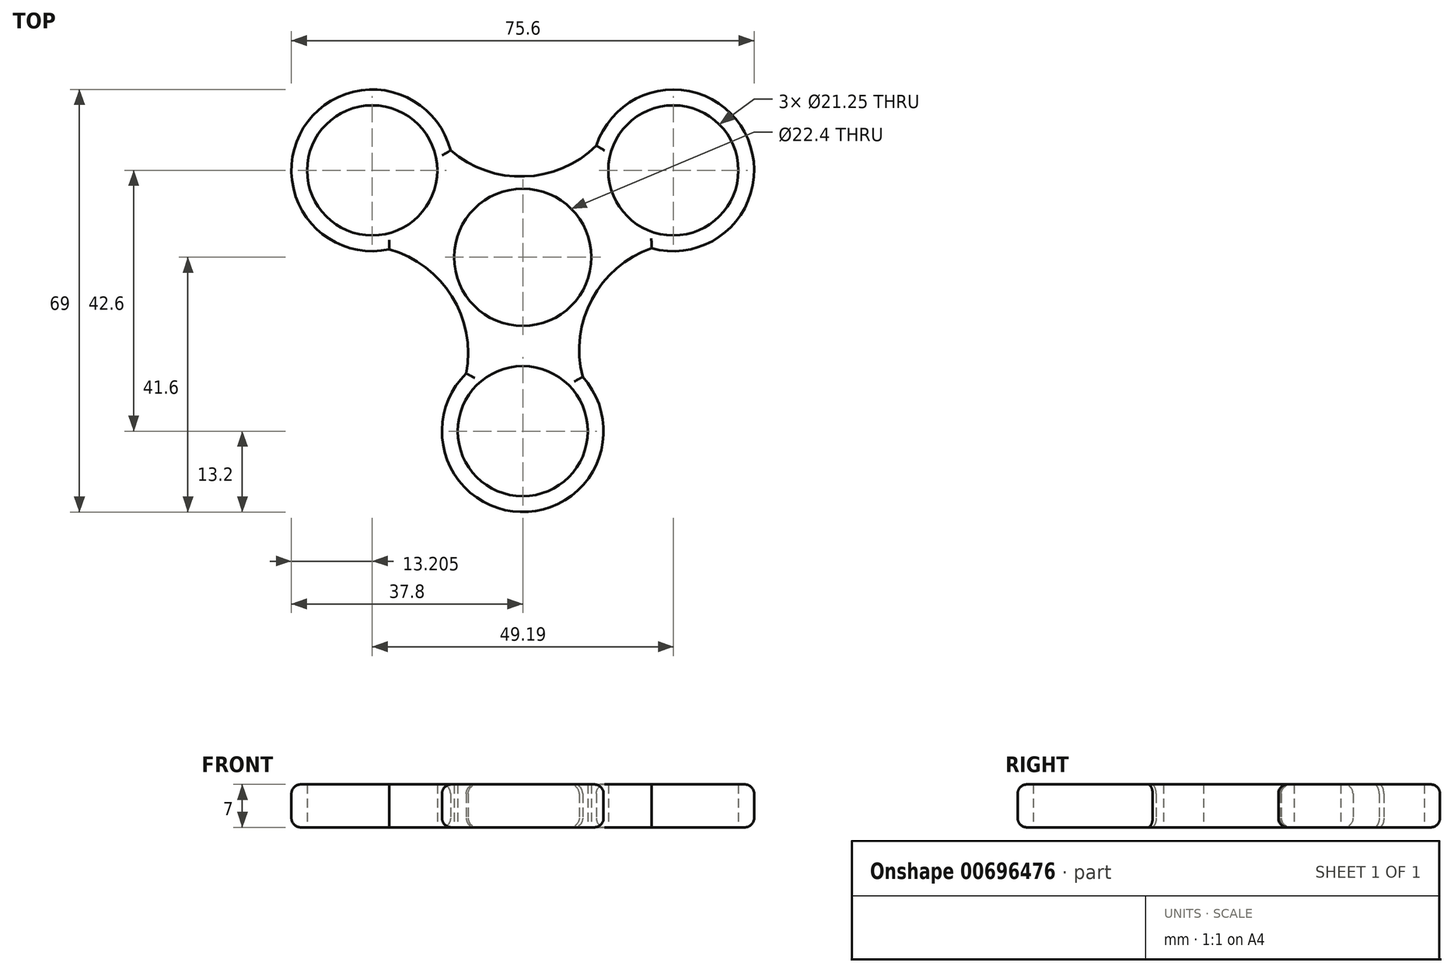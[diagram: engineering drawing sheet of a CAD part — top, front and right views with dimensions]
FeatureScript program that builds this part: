
annotation { "Feature Type Name" : "Feature", "Feature Type Description" : "" }
export const myFeature = defineFeature(function(context is Context, id is Id, definition is map)
    precondition{}
    {
        {
            var Q0;
            Q0=qCreatedBy(makeId("Top.planeOp"),FACE);
            var sketch = newSketch(context, id + "F0", { "sketchPlane" : qUnion([Q0])});
            skCircle(sketch, "E0", {"center": v(0, 0) * mm, "radius": 11.2 * mm});
            skArc(sketch, "E1", {"start": v(-11.43, -6.6) * mm, "mid": v(-11.37, -6.71) * mm, "end": v(-11.3, -6.83) * mm});
            skArc(sketch, "E2", {"start": v(-9.23, -18.96) * mm, "mid": v(-0.4, -41.6) * mm, "end": v(9.78, -19.54) * mm});
            skCircle(sketch, "E3", {"center": v(0, -28.4) * mm, "radius": 10.62 * mm});
            skPoint(sketch, "E4.start.orphan", {"position": v(0, -13.2) * mm});
            skCircle(sketch, "E5.1.0", {"center": v(24.6, 14.2) * mm, "radius": 10.62 * mm});
            skArc(sketch, "E5.1.1", {"start": v(21.04, 1.49) * mm, "mid": v(36.22, 20.45) * mm, "end": v(12.03, 18.24) * mm});
            skCircle(sketch, "E5.2.0", {"center": v(-24.6, 14.2) * mm, "radius": 10.62 * mm});
            skArc(sketch, "E5.2.1", {"start": v(-11.8, 17.47) * mm, "mid": v(-35.82, 21.14) * mm, "end": v(-21.81, 1.3) * mm});
            skArc(sketch, "E6", {"start": v(-11.8, 17.47) * mm, "mid": v(0.26, 13.2) * mm, "end": v(12.03, 18.24) * mm});
            skArc(sketch, "E7.1.0", {"start": v(-9.23, -18.96) * mm, "mid": v(-11.57, -6.38) * mm, "end": v(-21.81, 1.3) * mm});
            skArc(sketch, "E7.2.0", {"start": v(21.04, 1.49) * mm, "mid": v(11.3, -6.83) * mm, "end": v(9.78, -19.54) * mm});
            skArc(sketch, "E8.trimOffspring", {"start": v(0, 13.2) * mm, "mid": v(-0.13, 13.2) * mm, "end": v(-0.26, 13.2) * mm});
            skArc(sketch, "E9.trimOffspring", {"start": v(11.43, -6.6) * mm, "mid": v(11.5, -6.49) * mm, "end": v(11.56, -6.37) * mm});
            skPoint(sketch, "E10.start.orphan", {"position": v(13.2, 0) * mm});
            skPoint(sketch, "E11.start.orphan", {"position": v(-13.2, 0) * mm});
            skPoint(sketch, "E12.start.orphan", {"position": v(0, 15.2) * mm});
            skSolve(sketch);
        }
        {
            var Q0;
            Q0=makeQuery(id+"F0.imprint","IMPRINT",FACE,{"disambiguationData":[TD([[makeQuery(id+"F0.imprint","IMPRINT",EDGE,{"derivedFrom":sQuery(id+"F0.wireOp",EDGE,"E0")}),-1.0]])]});
            extrude(context, id + "F1", {"entities" : qUnion([Q0]), "depth" : 7 * mm, "offsetDistance" : 25 * mm});
        }
        {
            var Q0;
            Q0=makeQuery(id+"F1.opExtrude","CAP_EDGE",EDGE,{"disambiguationData":[OSD([sQuery(id+"F0.wireOp",EDGE,"E5.2.1")])],"isStart":false});
            var Q1;
            Q1=makeQuery(id+"F1.opExtrude","CAP_EDGE",EDGE,{"disambiguationData":[OSD([sQuery(id+"F0.wireOp",EDGE,"E6")])],"isStart":false});
            var Q2;
            Q2=makeQuery(id+"F1.opExtrude","CAP_EDGE",EDGE,{"disambiguationData":[OSD([sQuery(id+"F0.wireOp",EDGE,"E7.1.0")])],"isStart":false});
            var Q3;
            Q3=makeQuery(id+"F1.opExtrude","CAP_EDGE",EDGE,{"disambiguationData":[OSD([sQuery(id+"F0.wireOp",EDGE,"E5.1.1")])],"isStart":false});
            var Q4;
            Q4=makeQuery(id+"F1.opExtrude","CAP_EDGE",EDGE,{"disambiguationData":[OSD([sQuery(id+"F0.wireOp",EDGE,"E7.2.0")])],"isStart":false});
            var Q5;
            Q5=makeQuery(id+"F1.opExtrude","CAP_EDGE",EDGE,{"disambiguationData":[OSD([sQuery(id+"F0.wireOp",EDGE,"E2")])],"isStart":false});
            var Q6;
            Q6=makeQuery(id+"F1.opExtrude","CAP_EDGE",EDGE,{"disambiguationData":[OSD([sQuery(id+"F0.wireOp",EDGE,"E5.2.1")])],"isStart":true});
            var Q7;
            Q7=makeQuery(id+"F1.opExtrude","CAP_EDGE",EDGE,{"disambiguationData":[OSD([sQuery(id+"F0.wireOp",EDGE,"E6")])],"isStart":true});
            var Q8;
            Q8=makeQuery(id+"F1.opExtrude","CAP_EDGE",EDGE,{"disambiguationData":[OSD([sQuery(id+"F0.wireOp",EDGE,"E7.1.0")])],"isStart":true});
            var Q9;
            Q9=makeQuery(id+"F1.opExtrude","CAP_EDGE",EDGE,{"disambiguationData":[OSD([sQuery(id+"F0.wireOp",EDGE,"E2")])],"isStart":true});
            var Q10;
            Q10=makeQuery(id+"F1.opExtrude","CAP_EDGE",EDGE,{"disambiguationData":[OSD([sQuery(id+"F0.wireOp",EDGE,"E7.2.0")])],"isStart":true});
            var Q11;
            Q11=makeQuery(id+"F1.opExtrude","CAP_EDGE",EDGE,{"disambiguationData":[OSD([sQuery(id+"F0.wireOp",EDGE,"E5.1.1")])],"isStart":true});
            fillet(context, id + "F2", {"entities" : qUnion([Q0, Q1, Q2, Q3, Q4, Q5, Q6, Q7, Q8, Q9, Q10, Q11]), "radius" : 1.5 * mm, "tangentPropagation" : true, "allowEdgeOverflow" : false});
        }
    });
